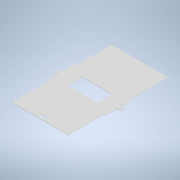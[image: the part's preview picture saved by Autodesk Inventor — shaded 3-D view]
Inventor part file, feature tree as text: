
AUTODESK INVENTOR PART (.ipt)
format: ipt  version: 2022 (Build 260153000, 153)  size: 161,280 bytes
history: native  units: mm
features: other x1, extrude x1, sketch x1
ambient origin geometry x8: Origin, YZ Plane, XZ Plane, XY Plane, X Axis, Y Axis, Z Axis, Center Point
bodies: Body1 (feature_tree)
feature tree (3):
  other  "Твердое тело1"
  extrude  "Выдавливание1"  Depth=0.5mm TaperAngle=0.0deg
  sketch  "Эскиз1"
